# Revit family: 359702
name_source: partatom
category: Specialty Equipment
revit_build: Autodesk Revit 2013 (Build: 20120221_2030(x64)
units: mm (PartAtom-declared; Revit-internal decimal feet)

## types (1)
- 359702
    Assembly Code = C1030200
    Dimensions = 290mm x 225mm x 390mm
    Manufacturer = FRANKE KITCHEN SYSTEMS (PTY) LTD
    Material = Grade 304 18/10
    Model = Electric Paper Towel Dispenser CHRX630
    Product Code = 359702
    Specification = Electronic paper towel dispenser for wall mounting, manufactured from Stainless Steel. Deep drawn cover with cylinder lock and standard Franke key, infrared sensor activity for non-touch operation, intergrated tear-off edge, four standard D 1.5 V batteries, maintenance free and easy paper roll change mechanism, for rolls with maxium width 210mm and maximum diameter 220mm, paper length adjustable to 200, 250 and 300mm. Includes Stainless Steel screws and dowels.

## geometry (parser evidence)
native form markers: Sweep x1
no freeform markers — native parametric forms only
